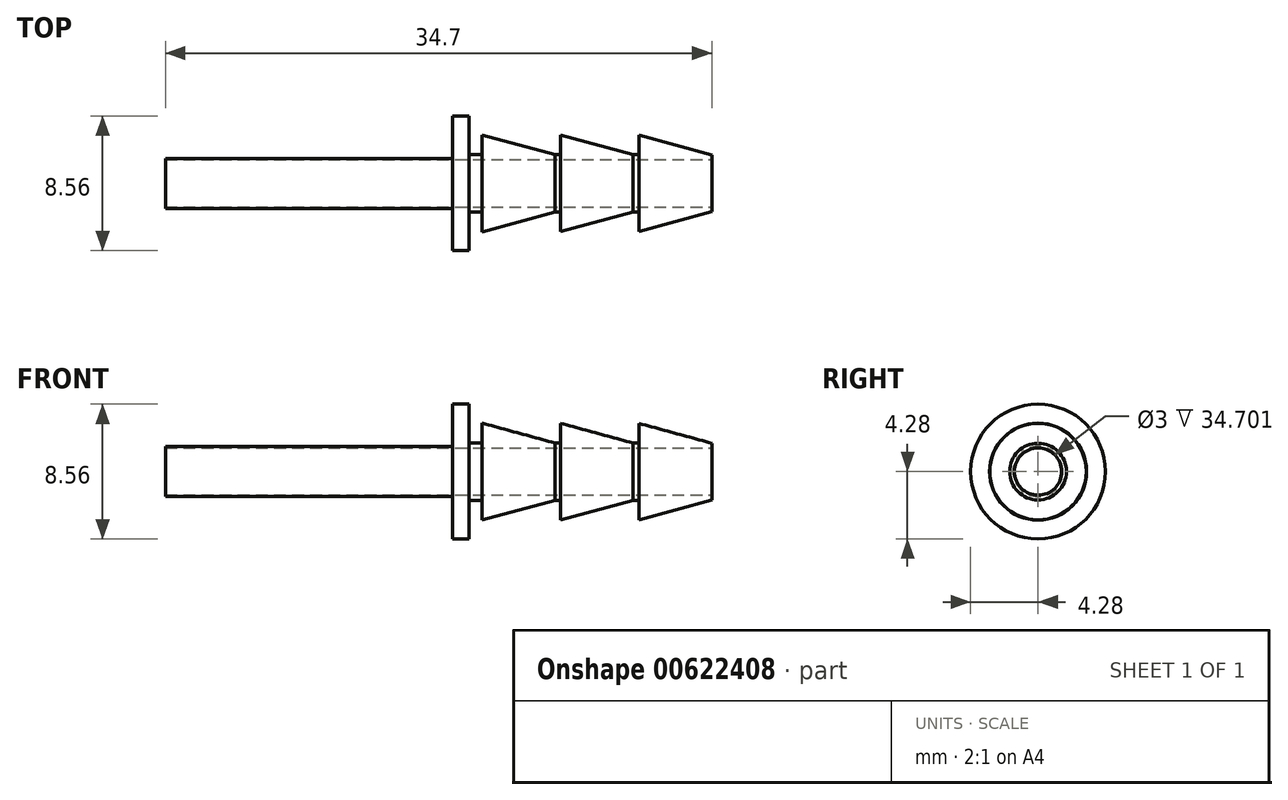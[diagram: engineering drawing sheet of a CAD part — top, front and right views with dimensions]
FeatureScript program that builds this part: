
annotation { "Feature Type Name" : "Feature", "Feature Type Description" : "" }
export const myFeature = defineFeature(function(context is Context, id is Id, definition is map)
    precondition{}
    {
        {
            var Q0;
            Q0=qCreatedBy(makeId("Front.planeOp"),FACE);
            var sketch = newSketch(context, id + "F0", { "sketchPlane" : qUnion([Q0])});
            skLineSegment(sketch, "E0", {"start": v(-18.23, 0) * mm, "end": v(-18.23, 1.59) * mm});
            skLineSegment(sketch, "E1", {"start": v(-18.23, 1.59) * mm, "end": v(0, 1.59) * mm});
            skLineSegment(sketch, "E2", {"start": v(0, 1.59) * mm, "end": v(0, 4.28) * mm});
            skLineSegment(sketch, "E3", {"start": v(0, 4.28) * mm, "end": v(1.04, 4.28) * mm});
            skLineSegment(sketch, "E4", {"start": v(1.04, 4.28) * mm, "end": v(1.04, 1.82) * mm});
            skLineSegment(sketch, "E5", {"start": v(1.04, 1.82) * mm, "end": v(1.88, 1.82) * mm});
            skLineSegment(sketch, "E6", {"start": v(1.88, 1.82) * mm, "end": v(1.88, 3.08) * mm});
            skLineSegment(sketch, "E7", {"start": v(1.88, 1.82) * mm, "end": v(16.28, 1.82) * mm});
            skLineSegment(sketch, "E8", {"start": v(1.88, 3.08) * mm, "end": v(6.5, 1.82) * mm});
            skLineSegment(sketch, "E9.1.0.0", {"start": v(6.86, 1.81) * mm, "end": v(6.86, 3.07) * mm});
            skLineSegment(sketch, "E9.1.0.1", {"start": v(6.02, 1.81) * mm, "end": v(6.86, 1.81) * mm});
            skLineSegment(sketch, "E9.1.0.2", {"start": v(6.86, 3.07) * mm, "end": v(11.48, 1.81) * mm});
            skLineSegment(sketch, "E9.2.0.0", {"start": v(11.84, 1.8) * mm, "end": v(11.84, 3.06) * mm});
            skLineSegment(sketch, "E9.2.0.1", {"start": v(11, 1.8) * mm, "end": v(11.84, 1.8) * mm});
            skLineSegment(sketch, "E9.2.0.2", {"start": v(11.84, 3.06) * mm, "end": v(16.47, 1.8) * mm});
            skLineSegment(sketch, "E9.direction1", {"start": v(1.04, 1.82) * mm, "end": v(6.02, 1.81) * mm, "construction": true});
            skLineSegment(sketch, "E10", {"start": v(16.47, 1.8) * mm, "end": v(16.47, 0) * mm});
            skLineSegment(sketch, "E11", {"start": v(-18.23, 0) * mm, "end": v(16.47, 0) * mm});
            skSolve(sketch);
        }
        {
            var Q0;
            {var subQ0=sQuery(id+"F0.wireOp",EDGE,"E9.1.0.0");var subQ1=sQuery(id+"F0.wireOp",EDGE,"E7");var subQ2=makeQuery(id+"F0.imprint","INTERSECT",VERTEX,{"derivedFrom":[subQ1,subQ0]});Q0=makeQuery(id+"F0.imprint","IMPRINT",FACE,{"disambiguationData":[TD([[makeQuery(id+"F0.imprint","IMPRINT",EDGE,{"disambiguationData":[TD([[subQ2,-1.0]])],"derivedFrom":subQ1}),1.0]])]});}
            var Q1;
            Q1=makeQuery(id+"F0.imprint","IMPRINT",FACE,{"disambiguationData":[TD([[makeQuery(id+"F0.imprint","IMPRINT",EDGE,{"derivedFrom":sQuery(id+"F0.wireOp",EDGE,"E0")}),-1.0]])]});
            var Q2;
            {var subQ0=sQuery(id+"F0.wireOp",EDGE,"E6");Q2=makeQuery(id+"F0.imprint","IMPRINT",FACE,{"disambiguationData":[TD([[makeQuery(id+"F0.imprint","IMPRINT",EDGE,{"derivedFrom":subQ0}),-1.0]])]});}
            var Q3;
            Q3=sQuery(id+"F0.wireOp",EDGE,"E11");
            revolve(context, id + "F1", {"entities" : qUnion([Q0, Q1, Q2]), "axis" : qUnion([Q3]), "revolveType" : RevolveType.FULL});
        }
        {
            var Q0;
            Q0=makeQuery(id+"F1.opRevolve","SWEPT_FACE",FACE,{"disambiguationData":[OSD([sQuery(id+"F0.wireOp",EDGE,"E10")])]});
            var sketch = newSketch(context, id + "F2", { "sketchPlane" : qUnion([Q0])});
            skCircle(sketch, "E12", {"center": v(0, 0) * mm, "radius": 1.5 * mm});
            skSolve(sketch);
        }
        {
            var Q0;
            Q0=makeQuery(id+"F2.imprint","IMPRINT",FACE,{"disambiguationData":[TD([[makeQuery(id+"F2.imprint","IMPRINT",EDGE,{"derivedFrom":sQuery(id+"F2.wireOp",EDGE,"E12")}),1.0]])]});
            extrude(context, id + "F3", {"entities" : qUnion([Q0]), "operationType" : NewBodyOperationType.REMOVE, "oppositeDirection" : true, "depth" : 48.2 * mm, "offsetDistance" : 25.4 * mm});
        }
    });
